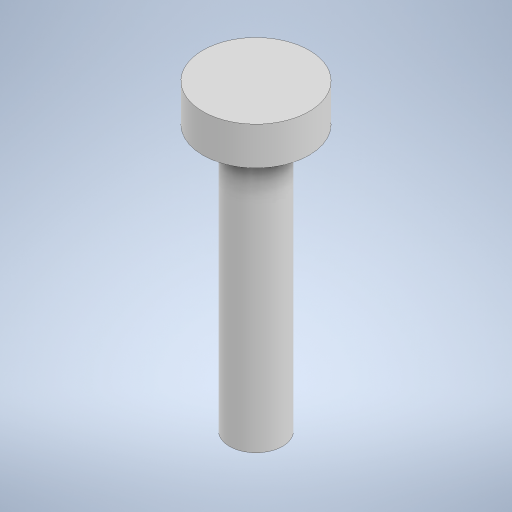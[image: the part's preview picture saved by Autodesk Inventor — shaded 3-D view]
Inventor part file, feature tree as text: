
AUTODESK INVENTOR PART (.ipt)
format: ipt  version: 2024 (Build 280153000, 153)  size: 240,128 bytes
history: native  units: mm
features: extrude x2, sketch x2
ambient origin geometry x8: Origin, YZ Plane, XZ Plane, XY Plane, X Axis, Y Axis, Z Axis, Center Point
bodies: Solid1 (feature_tree)
feature tree (4):
  extrude  "Extrusion1"  Depth=2.5mm TaperAngle=0.0deg
  extrude  "Extrusion2"  Depth=17.5mm TaperAngle=0.0deg
  sketch  "Sketch1"  dims[d0=7.0mm d1=2.5mm d2=0.0mm]
  sketch  "Sketch2"  dims[d3=3.5mm d4=17.5mm d5=0.0mm]
